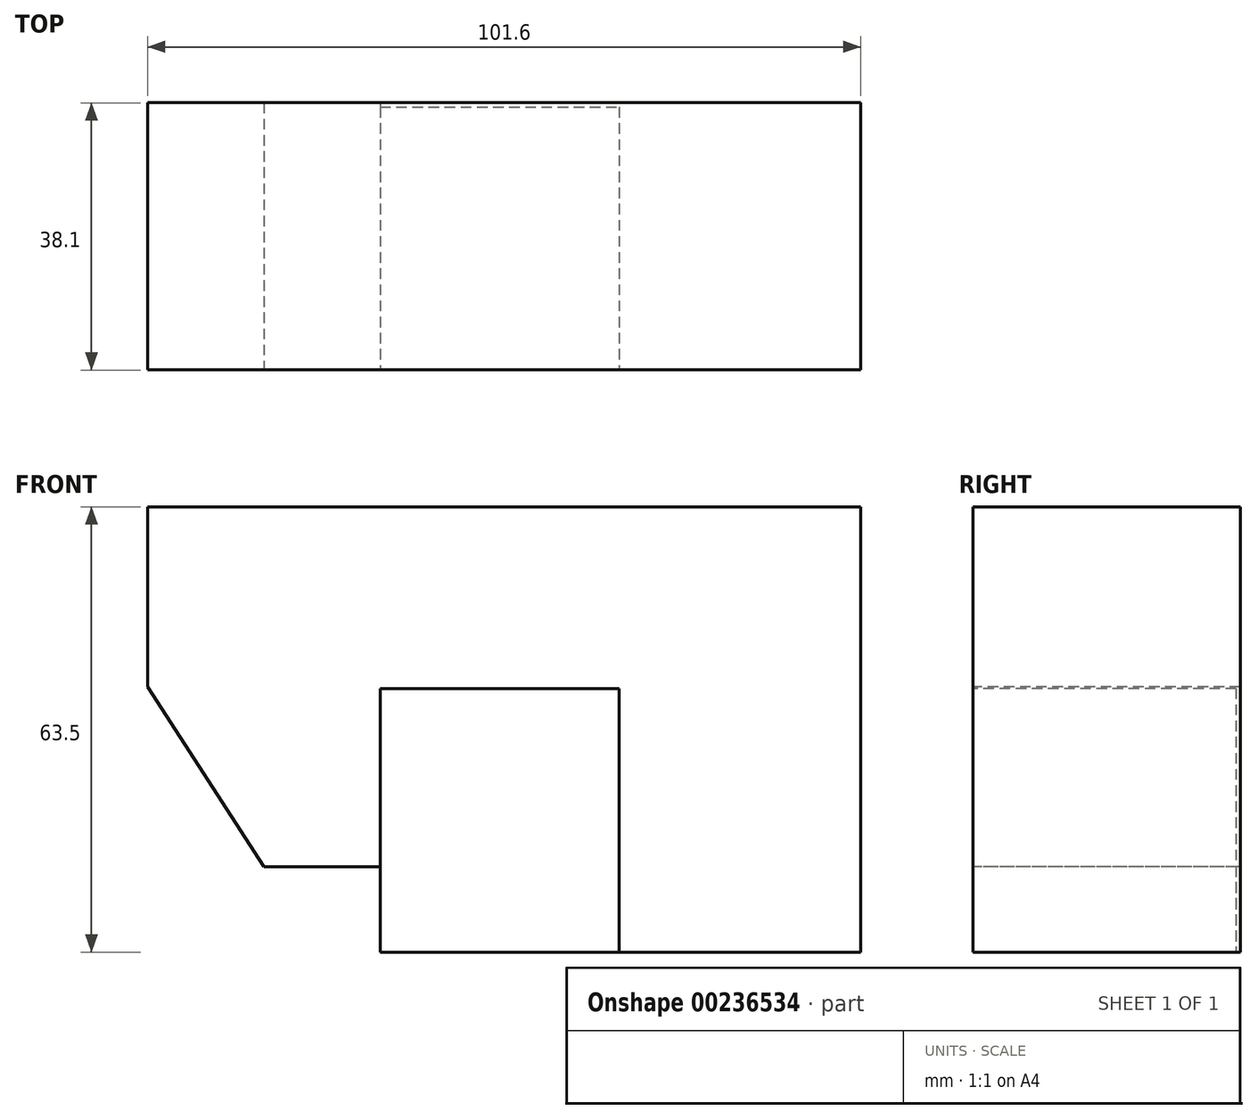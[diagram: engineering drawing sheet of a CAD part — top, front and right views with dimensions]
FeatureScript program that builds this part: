
annotation { "Feature Type Name" : "Feature", "Feature Type Description" : "" }
export const myFeature = defineFeature(function(context is Context, id is Id, definition is map)
    precondition{}
    {
        {
            var Q0;
            Q0=qCreatedBy(makeId("Top.planeOp"),FACE);
            var sketch = newSketch(context, id + "F0", { "sketchPlane" : qUnion([Q0])});
            skLineSegment(sketch, "E0.bottom", {"start": v(-48.09, 11.2) * mm, "end": v(53.51, 11.2) * mm});
            skLineSegment(sketch, "E0.top", {"start": v(-48.09, -26.9) * mm, "end": v(53.51, -26.9) * mm});
            skLineSegment(sketch, "E0.left", {"start": v(-48.09, 11.2) * mm, "end": v(-48.09, -26.9) * mm});
            skLineSegment(sketch, "E0.right", {"start": v(53.51, 11.2) * mm, "end": v(53.51, -26.9) * mm});
            skSolve(sketch);
        }
        {
            var Q0;
            Q0=makeQuery(id+"F0.imprint","IMPRINT",FACE,{"disambiguationData":[TD([[makeQuery(id+"F0.imprint","IMPRINT",EDGE,{"derivedFrom":sQuery(id+"F0.wireOp",EDGE,"E0.bottom")}),-1.0]])]});
            var sketch = newSketch(context, id + "F1", { "sketchPlane" : qUnion([Q0])});
            skLineSegment(sketch, "E1.bottom", {"start": v(-14.97, 10.58) * mm, "end": v(19.1, 10.58) * mm});
            skLineSegment(sketch, "E1.top", {"start": v(-14.97, -27.62) * mm, "end": v(19.1, -27.62) * mm});
            skLineSegment(sketch, "E1.left", {"start": v(-14.97, 10.58) * mm, "end": v(-14.97, -27.62) * mm});
            skLineSegment(sketch, "E1.right", {"start": v(19.1, 10.58) * mm, "end": v(19.1, -27.62) * mm});
            skLineSegment(sketch, "E2.bottom", {"start": v(19.1, -27.62) * mm, "end": v(36.65, -27.62) * mm});
            skLineSegment(sketch, "E2.top", {"start": v(19.1, 10.58) * mm, "end": v(36.65, 10.58) * mm});
            skLineSegment(sketch, "E2.left", {"start": v(19.1, -27.62) * mm, "end": v(19.1, 10.58) * mm});
            skLineSegment(sketch, "E2.right", {"start": v(36.65, -27.62) * mm, "end": v(36.65, 10.58) * mm});
            skSolve(sketch);
        }
        {
            var Q0;
            Q0=makeQuery(id+"F0.imprint","IMPRINT",FACE,{"disambiguationData":[TD([[makeQuery(id+"F0.imprint","IMPRINT",EDGE,{"derivedFrom":sQuery(id+"F0.wireOp",EDGE,"E0.bottom")}),-1.0]])]});
            extrude(context, id + "F2", {"entities" : qUnion([Q0]), "depth" : 63.5 * mm});
        }
        {
            var Q0;
            {var subQ0=sQuery(id+"F1.wireOp",EDGE,"E1.top");Q0=makeQuery(id+"F1.imprint","IMPRINT",FACE,{"disambiguationData":[TD([[makeQuery(id+"F1.imprint","IMPRINT",EDGE,{"derivedFrom":subQ0}),1.0]])]});}
            var Q1;
            {var subQ0=sQuery(id+"F1.wireOp",EDGE,"E1.bottom");Q1=makeQuery(id+"F1.imprint","IMPRINT",FACE,{"disambiguationData":[TD([[makeQuery(id+"F1.imprint","IMPRINT",EDGE,{"derivedFrom":subQ0}),-1.0]])]});}
            var Q2;
            Q2=sQuery(id+"F1.wireOp",EDGE,"E2.left");
            var Q3;
            Q3=sQuery(id+"F1.wireOp",EDGE,"E1.bottom");
            var Q4;
            Q4=sQuery(id+"F1.wireOp",EDGE,"E1.left");
            var Q5;
            Q5=sQuery(id+"F1.wireOp",EDGE,"E1.top");
            extrude(context, id + "F3", {"entities" : qUnion([Q0, Q1]), "operationType" : NewBodyOperationType.REMOVE, "surfaceEntities" : qUnion([Q2, Q3, Q4, Q5]), "depth" : 37.6 * mm});
        }
        {
            var Q0;
            Q0=makeQuery(id+"F2.opExtrude","CAP_FACE",FACE,{"disambiguationData":[OSD([sQuery(id+"F0.wireOp",EDGE,"E0.bottom"),sQuery(id+"F0.wireOp",EDGE,"E0.top"),sQuery(id+"F0.wireOp",EDGE,"E0.left"),sQuery(id+"F0.wireOp",EDGE,"E0.right")])],"isStart":true});
            var sketch = newSketch(context, id + "F4", { "sketchPlane" : qUnion([Q0])});
            skLineSegment(sketch, "E3.bottom", {"start": v(-14.97, -11.2) * mm, "end": v(-48.09, -11.2) * mm});
            skLineSegment(sketch, "E3.top", {"start": v(-14.97, 26.9) * mm, "end": v(-48.09, 26.9) * mm});
            skLineSegment(sketch, "E3.left", {"start": v(-14.97, -11.2) * mm, "end": v(-14.97, 26.9) * mm});
            skLineSegment(sketch, "E3.right", {"start": v(-48.09, -11.2) * mm, "end": v(-48.09, 26.9) * mm});
            skSolve(sketch);
        }
        {
            var Q0;
            {var subQ2=sQuery(id+"F4.wireOp",EDGE,"E3.bottom");Q0=makeQuery(id+"F4.imprint","IMPRINT",FACE,{"disambiguationData":[TD([[makeQuery(id+"F4.imprint","IMPRINT",EDGE,{"derivedFrom":subQ2}),1.0]])]});}
            extrude(context, id + "F5", {"entities" : qUnion([Q0]), "operationType" : NewBodyOperationType.REMOVE, "oppositeDirection" : true, "depth" : 12.2 * mm});
        }
        {
            var Q0;
            Q0=makeQuery(id+"F2.opExtrude","SWEPT_FACE",FACE,{"disambiguationData":[OSD([sQuery(id+"F0.wireOp",EDGE,"E0.top")])]});
            var sketch = newSketch(context, id + "F6", { "sketchPlane" : qUnion([Q0])});
            skLineSegment(sketch, "E4", {"start": v(-31.53, 12.2) * mm, "end": v(-48.09, 37.85) * mm});
            skLineSegment(sketch, "E5", {"start": v(-48.09, 37.85) * mm, "end": v(-48.09, 12.2) * mm});
            skLineSegment(sketch, "E6", {"start": v(-48.09, 12.2) * mm, "end": v(-31.53, 12.2) * mm});
            skSolve(sketch);
        }
        {
            var Q0;
            Q0=makeQuery(id+"F6.imprint","IMPRINT",FACE,{"disambiguationData":[TD([[makeQuery(id+"F6.imprint","IMPRINT",EDGE,{"derivedFrom":sQuery(id+"F6.wireOp",EDGE,"E4")}),1.0]])]});
            extrude(context, id + "F7", {"entities" : qUnion([Q0]), "operationType" : NewBodyOperationType.REMOVE, "oppositeDirection" : true, "depth" : 50.8 * mm});
        }
    });
